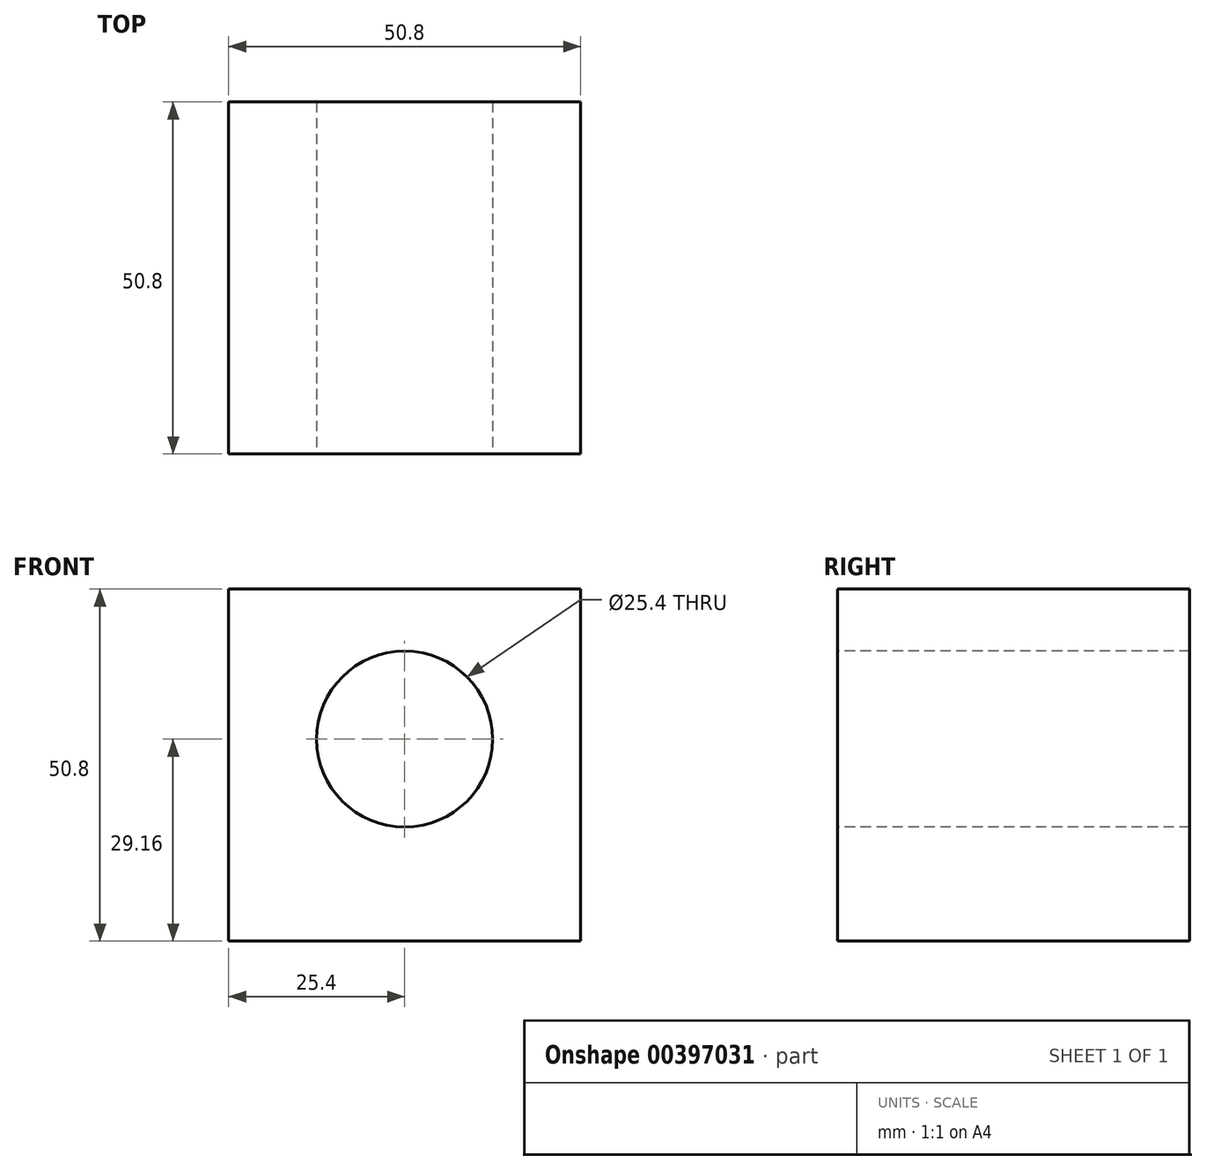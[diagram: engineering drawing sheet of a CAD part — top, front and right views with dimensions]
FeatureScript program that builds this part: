
annotation { "Feature Type Name" : "Feature", "Feature Type Description" : "" }
export const myFeature = defineFeature(function(context is Context, id is Id, definition is map)
    precondition{}
    {
        {
            var Q0;
            Q0=qCreatedBy(makeId("Front.planeOp"),FACE);
            var sketch = newSketch(context, id + "F0", { "sketchPlane" : qUnion([Q0])});
            skLineSegment(sketch, "E0.bottom", {"start": v(20.85, 21.64) * mm, "end": v(-29.95, 21.64) * mm});
            skLineSegment(sketch, "E0.top", {"start": v(20.85, -29.16) * mm, "end": v(-29.95, -29.16) * mm});
            skLineSegment(sketch, "E0.left", {"start": v(20.85, 21.64) * mm, "end": v(20.85, -29.16) * mm});
            skLineSegment(sketch, "E0.right", {"start": v(-29.95, 21.64) * mm, "end": v(-29.95, -29.16) * mm});
            skSolve(sketch);
        }
        {
            var Q0;
            Q0=makeQuery(id+"F0.imprint","IMPRINT",FACE,{"disambiguationData":[TD([[makeQuery(id+"F0.imprint","IMPRINT",EDGE,{"derivedFrom":sQuery(id+"F0.wireOp",EDGE,"E0.bottom")}),1.0]])]});
            extrude(context, id + "F1", {"entities" : qUnion([Q0]), "depth" : 50.8 * mm});
        }
        {
            var Q0;
            Q0=makeQuery(id+"F1.opExtrude","CAP_FACE",FACE,{"disambiguationData":[OSD([sQuery(id+"F0.wireOp",EDGE,"E0.bottom"),sQuery(id+"F0.wireOp",EDGE,"E0.top"),sQuery(id+"F0.wireOp",EDGE,"E0.left"),sQuery(id+"F0.wireOp",EDGE,"E0.right")])],"isStart":false});
            var sketch = newSketch(context, id + "F2", { "sketchPlane" : qUnion([Q0])});
            skPoint(sketch, "E1", {"position": v(-4.55, 0) * mm});
            skSolve(sketch);
        }
        {
            var Q0;
            Q0=sQuery(id+"F2.wireOp",VERTEX,"E1");
            var Q1;
            Q1=makeQuery(id+"F1.opExtrude","SWEPT_BODY",BODY,{"disambiguationData":[OSD([sQuery(id+"F0.wireOp",EDGE,"E0.bottom"),sQuery(id+"F0.wireOp",EDGE,"E0.top"),sQuery(id+"F0.wireOp",EDGE,"E0.left"),sQuery(id+"F0.wireOp",EDGE,"E0.right")])]});
            hole(context, id + "F3", {"style" : HoleStyle.SIMPLE, "endStyle" : HoleEndStyle.THROUGH, "holeDiameter" : 25.4 * mm, "isTappedThrough" : true, "tappedDepth" : 12.7 * mm, "tapClearance" : 3, "locations" : qUnion([Q0]), "scope" : qUnion([Q1])});
        }
    });
